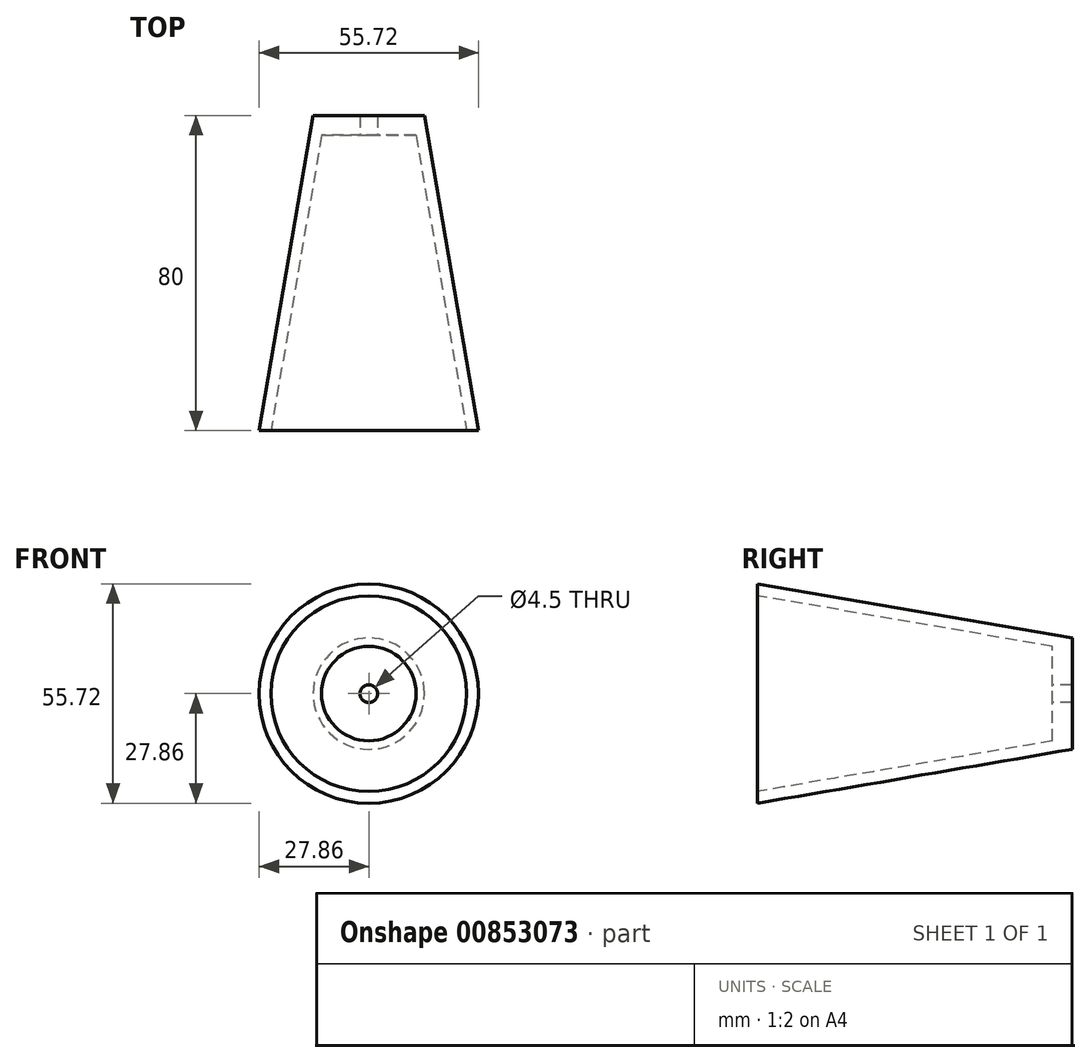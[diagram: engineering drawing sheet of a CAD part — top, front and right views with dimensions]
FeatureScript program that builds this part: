
annotation { "Feature Type Name" : "Feature", "Feature Type Description" : "" }
export const myFeature = defineFeature(function(context is Context, id is Id, definition is map)
    precondition{}
    {
        {
            var Q0;
            Q0=qCreatedBy(makeId("Right.planeOp"),FACE);
            var sketch = newSketch(context, id + "F0", { "sketchPlane" : qUnion([Q0])});
            skLineSegment(sketch, "E0", {"start": v(0, 0) * mm, "end": v(80, 0) * mm, "construction": true});
            skLineSegment(sketch, "E1", {"start": v(0, 0) * mm, "end": v(0, 24.86) * mm, "construction": true});
            skLineSegment(sketch, "E2", {"start": v(0, 24.86) * mm, "end": v(0, 27.86) * mm});
            skLineSegment(sketch, "E3", {"start": v(0, 27.86) * mm, "end": v(80, 14.14) * mm});
            skLineSegment(sketch, "E4", {"start": v(0, 24.86) * mm, "end": v(80, 11.14) * mm});
            skLineSegment(sketch, "E5", {"start": v(80, 11.14) * mm, "end": v(80, 14.14) * mm});
            skLineSegment(sketch, "E6", {"start": v(80, 0) * mm, "end": v(80, 2.25) * mm});
            skLineSegment(sketch, "E7", {"start": v(80, 2.25) * mm, "end": v(80, 11.14) * mm});
            skLineSegment(sketch, "E8", {"start": v(0, 0) * mm, "end": v(5, 0) * mm});
            skLineSegment(sketch, "E9", {"start": v(5, 0) * mm, "end": v(5, 27) * mm, "construction": true});
            skLineSegment(sketch, "E10", {"start": v(80, 2.25) * mm, "end": v(75, 2.25) * mm});
            skLineSegment(sketch, "E11", {"start": v(75, 2.25) * mm, "end": v(75, 12) * mm});
            skSolve(sketch);
        }
        {
            var Q0;
            {var subQ3=sQuery(id+"F0.wireOp",EDGE,"E2");Q0=makeQuery(id+"F0.imprint","IMPRINT",FACE,{"disambiguationData":[TD([[makeQuery(id+"F0.imprint","IMPRINT",EDGE,{"derivedFrom":subQ3}),-1.0]])]});}
            var Q1;
            {var subQ0=sQuery(id+"F0.wireOp",EDGE,"E7");Q1=makeQuery(id+"F0.imprint","IMPRINT",FACE,{"disambiguationData":[TD([[makeQuery(id+"F0.imprint","IMPRINT",EDGE,{"derivedFrom":subQ0}),1.0]])]});}
            var Q2;
            Q2=sQuery(id+"F0.wireOp",EDGE,"E0");
            revolve(context, id + "F1", {"surfaceOperationType" : NewSurfaceOperationType.NEW, "entities" : qUnion([Q0, Q1]), "axis" : qUnion([Q2]), "revolveType" : RevolveType.FULL});
        }
    });
